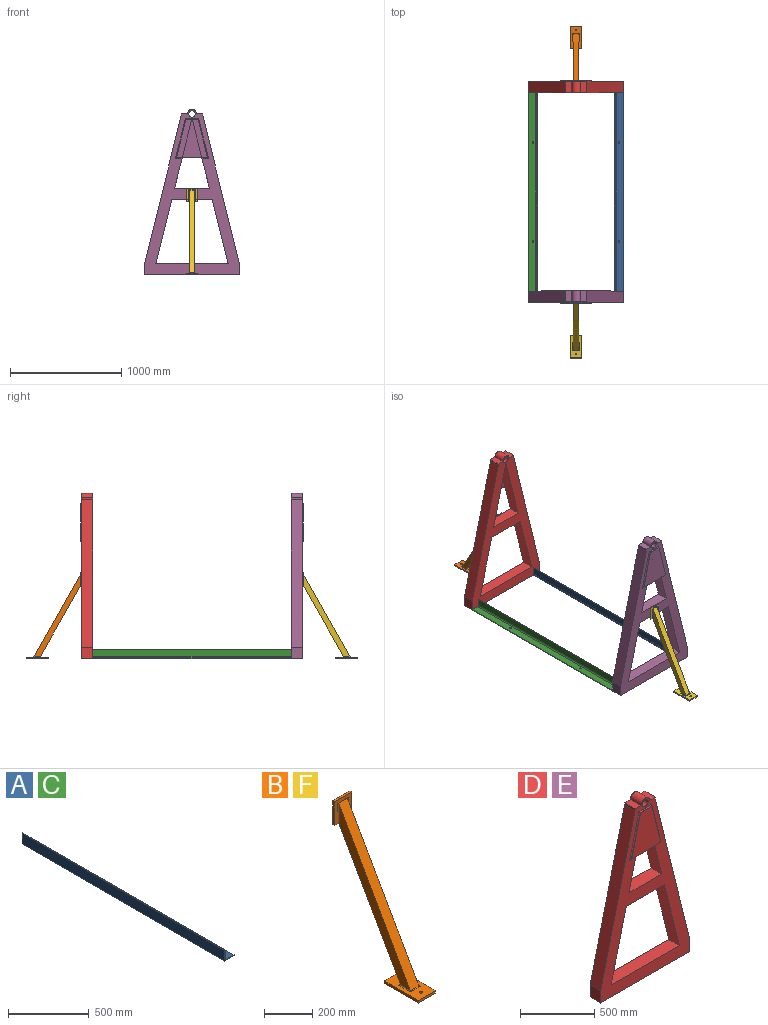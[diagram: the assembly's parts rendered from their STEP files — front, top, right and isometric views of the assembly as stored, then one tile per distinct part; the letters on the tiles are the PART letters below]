
ASSEMBLY  parts=6 mates=3
PART A: 11 faces, bbox 80x1778x80 mm
  f0: plane 1778x64mm, normal (1,0,0), area 113792mm2, adj f1,f6,f7,f8
  f1: plane 1778x6mm, normal (0,0,1), area 10668mm2, adj f0,f2,f7,f8
  f2: plane 1778x80mm, normal (-1,0,0), area 142240mm2, adj f1,f3,f7,f8
  f3: plane 1778x80mm, normal (0,0,-1), area 141932.1mm2, adj f2,f4,f7,f8,f9,f10
  f4: plane 1778x6mm, normal (1,0,0), area 10668mm2, adj f3,f5,f7,f8
  f5: plane 1778x64mm, normal (0,0,1), area 113484.1mm2, adj f4,f6,f7,f8,f9,f10
  f6: cylinder r=10mm len=1778mm, axis (0,1,0), area 27928.8mm2, adj f0,f5,f7,f8
  f7: plane 80x80mm, normal (0,-1,0), area 945.5mm2, adj f0,f1,f2,f3,f4,f5,f6
  f8: plane 80x80mm, normal (0,1,0), area 945.5mm2, adj f0,f1,f2,f3,f4,f5,f6
  f9: cylinder r=7mm len=14mm, axis (0,0,-1), area 263.9mm2, adj f3,f5
  f10: cylinder r=7mm len=14mm, axis (0,0,-1), area 263.9mm2, adj f3,f5
PART B: 25 faces, bbox 100x500x775 mm
  f0: plane 741.62x419.2mm, normal (0,-0.87,0.49), area 42609.1mm2, adj f2,f3,f18,f19,f20,f21,f22,f23
  f1: plane 634.12x358.43mm, normal (0,0.87,-0.49), area 36429mm2, adj f2,f3,f17,f22,f23,f24
  f2: plane 731.46x413.45mm, normal (-1,0,0), area 39094mm2, adj f0,f1,f17,f18,f22
  f3: plane 731.46x413.45mm, normal (1,0,0), area 39094mm2, adj f0,f1,f17,f19,f23
  f4: plane 120x100mm, normal (0,-1,0), area 5782.6mm2, adj f5,f7,f8,f9,f21,f22,f23
  f5: plane 100x10mm, normal (0,0,-1), area 1000mm2, adj f4,f6,f8,f9,f24
  f6: plane 120x100mm, normal (0,1,0), area 12000mm2, adj f5,f7,f8,f9
  f7: plane 100x10mm, normal (0,0,1), area 1000mm2, adj f4,f6,f8,f9
  f8: plane 120x10mm, normal (1,0,0), area 1200mm2, adj f4,f5,f6,f7
  f9: plane 120x10mm, normal (-1,0,0), area 1200mm2, adj f4,f5,f6,f7
  f10: plane 200x100mm, normal (0,0,1), area 15710.8mm2, adj f11,f13,f14,f15,f16,f17,f18,f19
  f11: plane 100x12mm, normal (0,-1,0), area 1200mm2, adj f10,f12,f14,f15
  f12: plane 200x100mm, normal (0,0,-1), area 19846.1mm2, adj f11,f13,f14,f15,f16
  f13: plane 100x12mm, normal (0,1,0), area 1200mm2, adj f10,f12,f14,f15
  f14: plane 200x12mm, normal (1,0,0), area 2400mm2, adj f10,f11,f12,f13
  f15: plane 200x12mm, normal (-1,0,0), area 2400mm2, adj f10,f11,f12,f13
  f16: cylinder r=7mm len=14mm, axis (0,0,1), area 527.8mm2, adj f10,f12
  f17: cylinder r=5mm len=60mm, axis (-1,0,0), area 549.9mm2, adj f1,f2,f3,f10,f18,f19
  f18: cylinder r=5mm len=68.92mm, axis (0,1,0), area 490.7mm2, adj f0,f2,f10,f17,f20
  f19: cylinder r=5mm len=68.92mm, axis (0,-1,0), area 490.7mm2, adj f0,f3,f10,f17,f20
  f20: cylinder r=5mm len=60mm, axis (1,0,0), area 291.5mm2, adj f0,f10,f18,f19
  f21: cylinder r=5mm len=60mm, axis (-1,0,0), area 147.9mm2, adj f0,f4,f22,f23
  f22: cylinder r=5mm len=111.77mm, axis (0,0,1), area 800.6mm2, adj f0,f1,f2,f4,f21,f24
  f23: cylinder r=5mm len=111.77mm, axis (0,0,-1), area 800.6mm2, adj f0,f1,f3,f4,f21,f24
  f24: cylinder r=5mm len=60mm, axis (-1,0,0), area 103.2mm2, adj f1,f5,f22,f23
PART C: same geometry as A
PART D: 32 faces, bbox 850x110x1480.5 mm
  f0: plane 1480.5x850mm, normal (0,-1,0), area 348380.6mm2, adj f1,f2,f3,f4,f5,f6,f7,f8
  f1: plane 624.5x156.19mm, normal (0.97,0,-0.24), area 64401.8mm2, adj f0,f2,f15,f19,f20,f21,f23,f29
  f2: plane 624.5x156.19mm, normal (-0.97,0,-0.24), area 64401.8mm2, adj f0,f1,f15,f19,f20,f21,f23,f26
  f3: plane 575x143.81mm, normal (-0.97,0,-0.24), area 59271mm2, adj f0,f4,f16,f19
  f4: plane 650x100mm, normal (0,0,1), area 65000mm2, adj f0,f3,f5,f19
  f5: plane 575x143.81mm, normal (0.97,0,-0.24), area 59271mm2, adj f0,f4,f16,f19
  f6: plane 100x56.51mm, normal (0,0,1), area 5651.2mm2, adj f0,f7,f17,f19
  f7: cylinder r=40.5mm len=100mm, axis (0,1,0), area 12723.5mm2, adj f0,f6,f8,f19
  f8: plane 100x56.51mm, normal (0,0,1), area 5651.2mm2, adj f0,f7,f9,f19
  f9: plane 100x16.24mm, normal (-1,0,0), area 1623.8mm2, adj f0,f8,f10,f19
  f10: plane 1323.76x327.99mm, normal (-0.97,0,0.24), area 136379mm2, adj f0,f9,f11,f19
  f11: plane 100x100mm, normal (-1,0,0), area 10000mm2, adj f0,f10,f12,f19
  f12: plane 850x100mm, normal (0,0,-1), area 85000mm2, adj f0,f11,f13,f19
  f13: plane 100x100mm, normal (1,0,0), area 10000mm2, adj f0,f12,f14,f19
  f14: plane 1323.76x327.99mm, normal (0.97,0,0.24), area 136379mm2, adj f0,f13,f17,f19
  f15: plane 312.37x100mm, normal (0,0,1), area 31237mm2, adj f0,f1,f2,f19
  f16: plane 362.39x100mm, normal (0,0,-1), area 36238.9mm2, adj f0,f3,f5,f19
  f17: plane 100x16.24mm, normal (1,0,0), area 1623.8mm2, adj f0,f6,f14,f19
  f18: cylinder r=28.5mm len=100mm, axis (0,1,0), area 17907.1mm2, adj f0,f19
  f19: plane 1480.5x850mm, normal (0,1,0), area 390595.6mm2, adj f1,f2,f3,f4,f5,f6,f7,f8
  f20: plane 339.73x174.68mm, normal (0,1,0), area 30479.1mm2, adj f1,f2,f21,f23
  f21: plane 107.73x10mm, normal (0,0,1), area 253.5mm2, adj f1,f2,f20,f22,f24,f25,f28,f29
  f22: plane 339.73x84.17mm, normal (-0.97,0,0.24), area 700mm2, adj f21,f23,f25,f30
  f23: plane 276.08x10mm, normal (0,0,-1), area 1949.6mm2, adj f1,f2,f20,f22,f24,f25,f26,f31
  f24: plane 339.73x84.17mm, normal (0.97,0,0.24), area 700mm2, adj f21,f23,f25,f27
  f25: plane 339.73x276.08mm, normal (0,-1,0), area 65195.4mm2, adj f21,f22,f23,f24
  f26: cylinder r=8mm len=60.92mm, axis (1,0,0), area 674.7mm2, adj f0,f2,f23,f27
  f27: cylinder r=8mm len=357.65mm, axis (-0.24,0,0.97), area 4473.5mm2, adj f0,f24,f26,f28
  f28: cylinder r=8mm len=59.75mm, axis (-1,0,0), area 684.8mm2, adj f0,f2,f21,f27
  f29: cylinder r=8mm len=59.75mm, axis (-1,0,0), area 684.8mm2, adj f0,f1,f21,f30
  f30: cylinder r=8mm len=357.65mm, axis (-0.24,0,-0.97), area 4473.5mm2, adj f0,f22,f29,f31
  f31: cylinder r=8mm len=60.92mm, axis (1,0,0), area 674.7mm2, adj f0,f1,f23,f30
PART E: same geometry as D
PART F: same geometry as B
PLACE A t=(-64.55,989.78,-695.7)mm
PLACE B rot(axis=(0,0,-1),180deg) t=(-437.43,1978.78,164.71)mm
PLACE C rot(axis=(0,0,-1),180deg) t=(-810.3,989.78,-695.7)mm
PLACE D rot(axis=(0,0,-1),180deg) t=(-437.43,1928.78,8.46)mm
PLACE E t=(-437.43,50.78,8.46)mm
PLACE F t=(-437.43,0.78,164.29)mm
MATE fastened F.f6 <-> E.f0  axis (0,1,0) through (-437.43,0.78,51.45)mm
MATE fastened D.f19 <-> C.f7  axis (0,-1,0) through (-862.43,1878.78,-723.55)mm
MATE fastened E.f19 <-> C.f8  axis (0,1,0) through (-862.43,100.78,-723.55)mm
